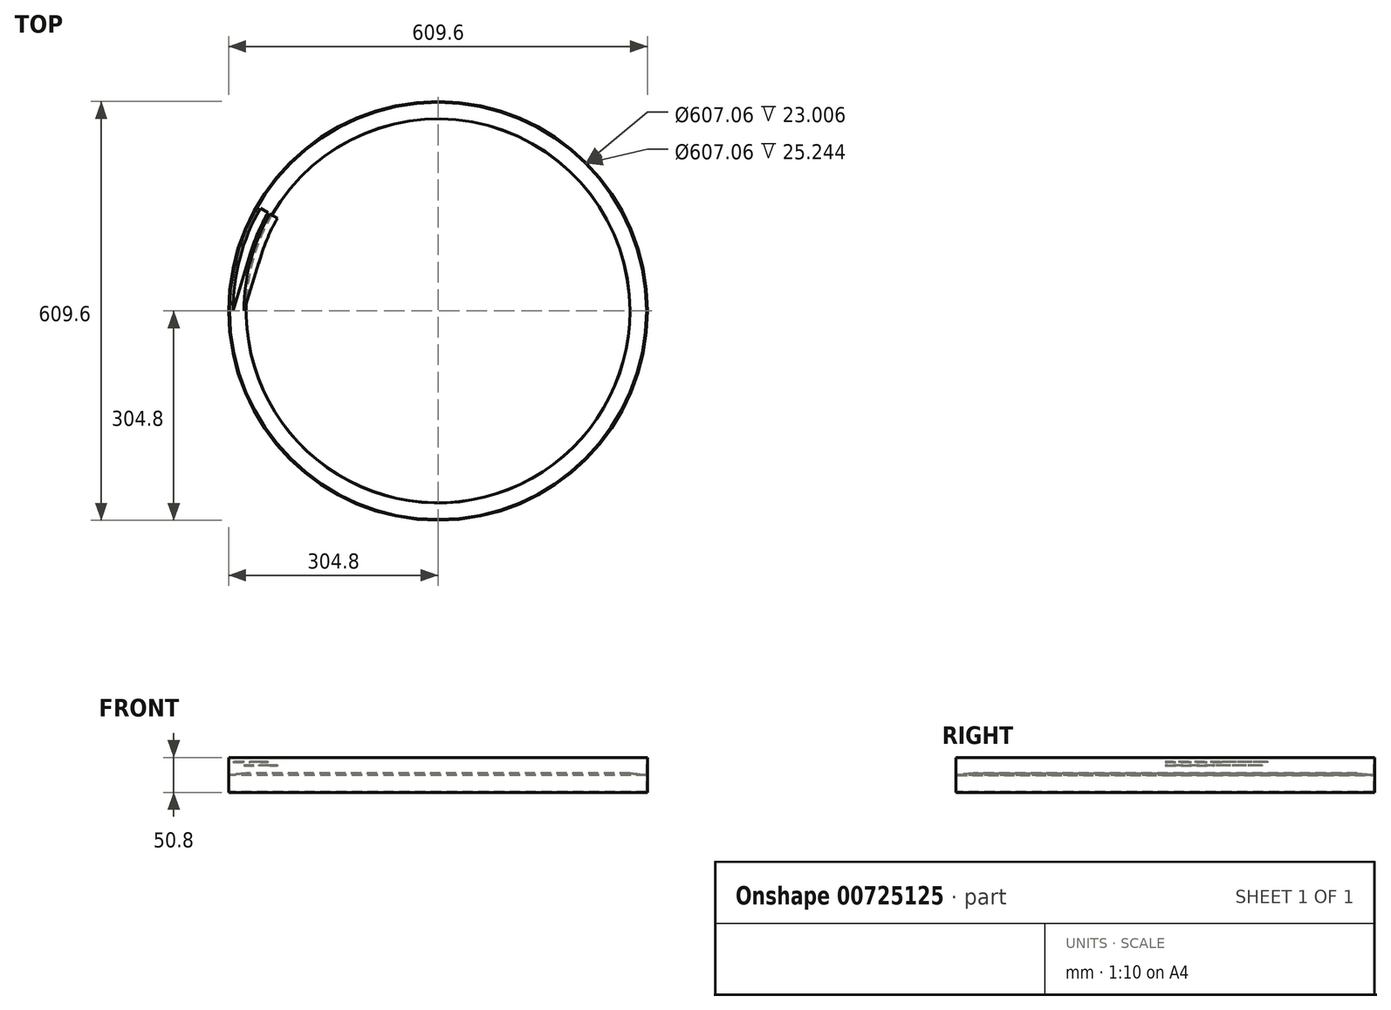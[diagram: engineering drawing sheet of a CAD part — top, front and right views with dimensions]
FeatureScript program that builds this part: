
annotation { "Feature Type Name" : "Feature", "Feature Type Description" : "" }
export const myFeature = defineFeature(function(context is Context, id is Id, definition is map)
    precondition{}
    {
        {
            var Q0;
            Q0=qCreatedBy(makeId("Front.planeOp"),FACE);
            var sketch = newSketch(context, id + "F0", { "sketchPlane" : qUnion([Q0])});
            skLineSegment(sketch, "E0.left", {"start": v(-304.8, -3.12) * mm, "end": v(-304.8, -28.52) * mm});
            skLineSegment(sketch, "E1", {"start": v(-279.4, 0) * mm, "end": v(-303.53, -2.96) * mm});
            skLineSegment(sketch, "E2", {"start": v(-279.4, 0) * mm, "end": v(-279.25, -1.26) * mm});
            skLineSegment(sketch, "E3", {"start": v(-279.25, -1.26) * mm, "end": v(-303.53, -4.24) * mm});
            skPoint(sketch, "E4.orphan", {"position": v(-304.8, 0) * mm});
            skLineSegment(sketch, "E5", {"start": v(-304.8, -3.12) * mm, "end": v(-304.8, 22.28) * mm});
            skLineSegment(sketch, "E6", {"start": v(-304.8, 22.28) * mm, "end": v(-303.53, 22.28) * mm});
            skLineSegment(sketch, "E7", {"start": v(-303.53, 22.28) * mm, "end": v(-303.53, -2.96) * mm});
            skLineSegment(sketch, "E8", {"start": v(-304.8, -28.52) * mm, "end": v(0, -28.52) * mm});
            skLineSegment(sketch, "E9", {"start": v(-303.53, -27.25) * mm, "end": v(-303.53, -4.24) * mm});
            skLineSegment(sketch, "E10", {"start": v(-303.53, -27.25) * mm, "end": v(0, -27.25) * mm});
            skLineSegment(sketch, "E11", {"start": v(0, -28.52) * mm, "end": v(0, -27.25) * mm});
            skSolve(sketch);
        }
        {
            var Q0;
            Q0=qCreatedBy(makeId("Front.planeOp"),FACE);
            var sketch = newSketch(context, id + "F1", { "sketchPlane" : qUnion([Q0])});
            skLineSegment(sketch, "E12", {"start": v(0, 40.5) * mm, "end": v(0, -62.38) * mm});
            skSolve(sketch);
        }
        {
            var Q0;
            Q0=makeQuery(id+"F0.imprint","IMPRINT",FACE,{"disambiguationData":[TD([[makeQuery(id+"F0.imprint","IMPRINT",EDGE,{"derivedFrom":sQuery(id+"F0.wireOp",EDGE,"E0.left")}),1.0]])]});
            var Q1;
            Q1=sQuery(id+"F1.wireOp",EDGE,"E12");
            revolve(context, id + "F2", {"surfaceOperationType" : NewSurfaceOperationType.NEW, "entities" : qUnion([Q0]), "axis" : qUnion([Q1]), "revolveType" : RevolveType.FULL});
        }
        {
            var Q0;
            Q0=qCreatedBy(makeId("Front.planeOp"),FACE);
            var sketch = newSketch(context, id + "F3", { "sketchPlane" : qUnion([Q0])});
            skLineSegment(sketch, "E13.bottom", {"start": v(-282.63, 11.43) * mm, "end": v(-269.93, 11.43) * mm});
            skLineSegment(sketch, "E13.top", {"start": v(-282.63, 10.16) * mm, "end": v(-269.93, 10.16) * mm});
            skLineSegment(sketch, "E13.left", {"start": v(-282.63, 11.43) * mm, "end": v(-282.63, 10.16) * mm});
            skLineSegment(sketch, "E13.right", {"start": v(-269.93, 11.43) * mm, "end": v(-269.93, 10.16) * mm});
            skLineSegment(sketch, "E14.bottom", {"start": v(-298.63, 16.5) * mm, "end": v(-285.93, 16.5) * mm});
            skLineSegment(sketch, "E14.top", {"start": v(-298.63, 15.24) * mm, "end": v(-285.93, 15.24) * mm});
            skLineSegment(sketch, "E14.left", {"start": v(-298.63, 16.5) * mm, "end": v(-298.63, 15.24) * mm});
            skLineSegment(sketch, "E14.right", {"start": v(-285.93, 16.5) * mm, "end": v(-285.93, 15.24) * mm});
            skSolve(sketch);
        }
        {
            var Q0;
            Q0 = qSketchRegion(id + "F3", true);
            var Q1;
            Q1=sQuery(id+"F1.wireOp",EDGE,"E12");
            revolve(context, id + "F4", {"surfaceOperationType" : NewSurfaceOperationType.NEW, "entities" : qUnion([Q0]), "axis" : qUnion([Q1]), "revolveType" : RevolveType.ONE_DIRECTION, "angle" : 30 * degree});
        }
        {
            var Q0;
            Q0=makeQuery(id+"F4.opRevolve","SWEPT_FACE",FACE,{"disambiguationData":[OSD([sQuery(id+"F3.wireOp",EDGE,"E14.bottom")])]});
            var sketch = newSketch(context, id + "F5", { "sketchPlane" : qUnion([Q0])});
            skLineSegment(sketch, "E15", {"start": v(-298.63, 0) * mm, "end": v(-273.77, 82.5) * mm});
            skLineSegment(sketch, "E16", {"start": v(-273.77, 82.5) * mm, "end": v(-285.93, 0) * mm});
            skLineSegment(sketch, "E17", {"start": v(-285.93, 0) * mm, "end": v(-298.63, 0) * mm});
            skSolve(sketch);
        }
        {
            var Q0;
            Q0=makeQuery(id+"F4.opRevolve","SWEPT_FACE",FACE,{"disambiguationData":[OSD([sQuery(id+"F3.wireOp",EDGE,"E13.bottom")])]});
            var sketch = newSketch(context, id + "F6", { "sketchPlane" : qUnion([Q0])});
            skLineSegment(sketch, "E18", {"start": v(-282.63, 0) * mm, "end": v(-260.73, 70.56) * mm});
            skPoint(sketch, "E18.endSnap0", {"position": v(-260.73, 69.86) * mm});
            skLineSegment(sketch, "E19", {"start": v(-260.73, 70.56) * mm, "end": v(-269.93, 0) * mm});
            skLineSegment(sketch, "E20", {"start": v(-269.93, 0) * mm, "end": v(-282.63, 0) * mm});
            skSolve(sketch);
        }
        {
            var Q0;
            Q0 = qSketchRegion(id + "F5", true);
            extrude(context, id + "F7", {"entities" : qUnion([Q0]), "operationType" : NewBodyOperationType.REMOVE, "endBound" : BoundingType.UP_TO_NEXT, "oppositeDirection" : true, "depth" : 25.4 * mm, "offsetDistance" : 25.4 * mm});
        }
        {
            var Q0;
            Q0 = qSketchRegion(id + "F6", true);
            extrude(context, id + "F8", {"entities" : qUnion([Q0]), "operationType" : NewBodyOperationType.REMOVE, "endBound" : BoundingType.UP_TO_NEXT, "oppositeDirection" : true, "depth" : 25.4 * mm, "offsetDistance" : 25.4 * mm});
        }
    });
